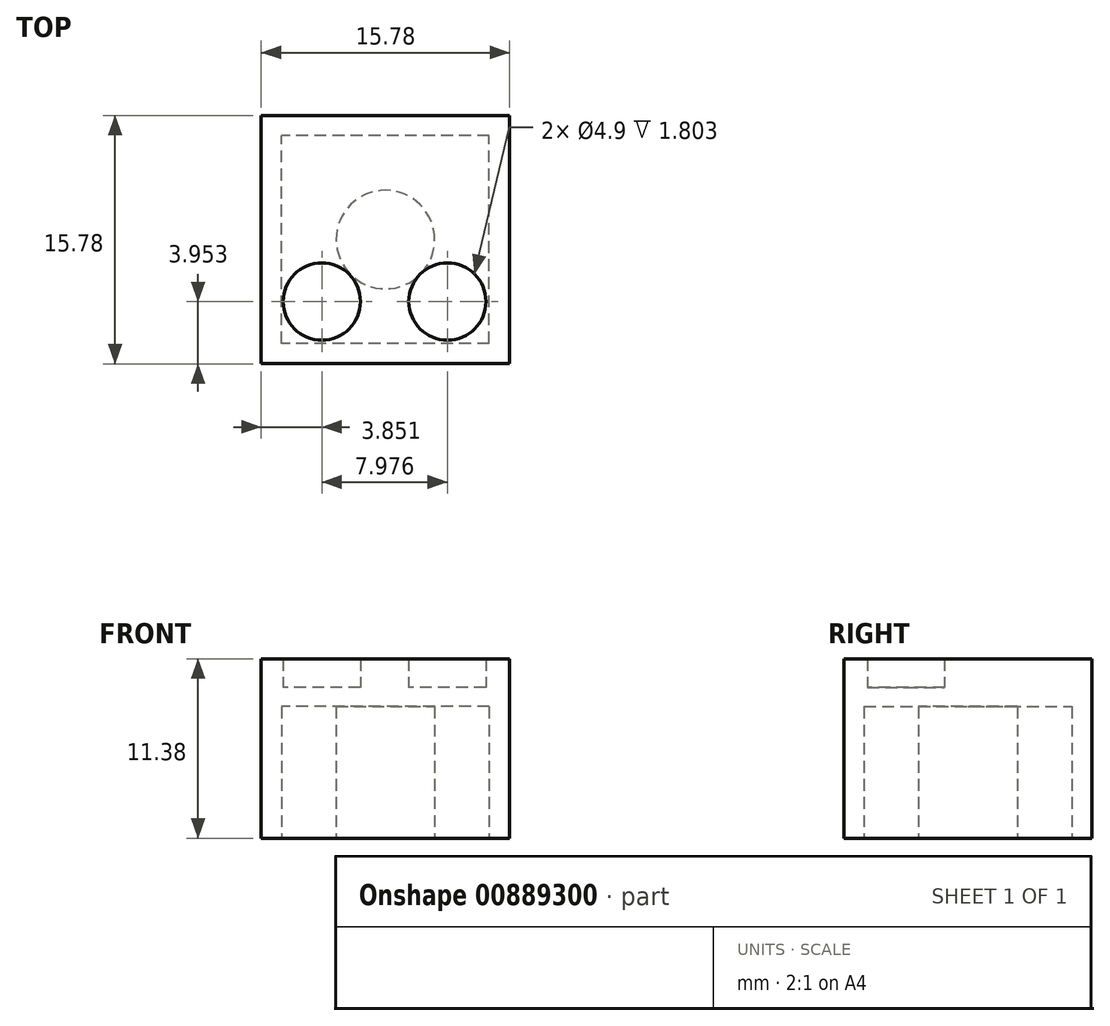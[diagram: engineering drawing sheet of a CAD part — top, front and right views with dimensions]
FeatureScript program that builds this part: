
annotation { "Feature Type Name" : "Feature", "Feature Type Description" : "" }
export const myFeature = defineFeature(function(context is Context, id is Id, definition is map)
    precondition{}
    {
        {
            var Q0;
            Q0=qCreatedBy(makeId("Top.planeOp"),FACE);
            var sketch = newSketch(context, id + "F0", { "sketchPlane" : qUnion([Q0])});
            skLineSegment(sketch, "E0.bottom", {"start": v(7.89, 7.89) * mm, "end": v(-7.89, 7.89) * mm});
            skLineSegment(sketch, "E0.top", {"start": v(7.89, -7.89) * mm, "end": v(-7.89, -7.89) * mm});
            skLineSegment(sketch, "E0.left", {"start": v(7.89, 7.89) * mm, "end": v(7.89, -7.89) * mm});
            skLineSegment(sketch, "E0.right", {"start": v(-7.89, 7.89) * mm, "end": v(-7.89, -7.89) * mm});
            skPoint(sketch, "E0.middle", {"position": v(0, 0) * mm});
            skSolve(sketch);
        }
        {
            var Q0;
            Q0 = qSketchRegion(id + "F2", true);
            var Q1;
            Q1 = qSketchRegion(id + "F0", true);
            extrude(context, id + "F1", {"entities" : qUnion([Q0, Q1]), "offsetDistance" : 25.4 * mm, "depth" : 9.58 * mm});
        }
        {
            var Q0;
            Q0=makeQuery(id+"F1.opExtrude","CAP_FACE",FACE,{"disambiguationData":[OSD([sQuery(id+"F0.wireOp",EDGE,"E0.bottom"),sQuery(id+"F0.wireOp",EDGE,"E0.top"),sQuery(id+"F0.wireOp",EDGE,"E0.left"),sQuery(id+"F0.wireOp",EDGE,"E0.right")])],"isStart":false});
            var sketch = newSketch(context, id + "F2", { "sketchPlane" : qUnion([Q0])});
            skCircle(sketch, "E1", {"center": v(-4.04, 3.94) * mm, "radius": 2.45 * mm});
            skCircle(sketch, "E2.1.0.0", {"center": v(3.94, 3.94) * mm, "radius": 2.45 * mm});
            skLineSegment(sketch, "E2.direction1", {"start": v(-4.04, 3.94) * mm, "end": v(3.94, 3.94) * mm, "construction": true});
            skCircle(sketch, "E3.MirrorC", {"center": v(-4.04, -3.94) * mm, "radius": 2.45 * mm});
            skCircle(sketch, "E4.MirrorC", {"center": v(3.94, -3.94) * mm, "radius": 2.45 * mm});
            skSolve(sketch);
        }
        {
            var Q0;
            Q0=makeQuery(id+"F2.imprint","IMPRINT",FACE,{"disambiguationData":[TD([[makeQuery(id+"F2.imprint","IMPRINT",EDGE,{"derivedFrom":sQuery(id+"F2.wireOp",EDGE,"E3.MirrorC")}),-1.0]])]});
            var Q1;
            Q1=makeQuery(id+"F2.imprint","IMPRINT",FACE,{"disambiguationData":[TD([[makeQuery(id+"F2.imprint","IMPRINT",EDGE,{"derivedFrom":sQuery(id+"F2.wireOp",EDGE,"E4.MirrorC")}),-1.0]])]});
            var Q2;
            Q2=makeQuery(id+"F2.imprint","IMPRINT",FACE,{"disambiguationData":[TD([[makeQuery(id+"F2.imprint","IMPRINT",EDGE,{"derivedFrom":sQuery(id+"F2.wireOp",EDGE,"E2.1.0.0")}),1.0]])]});
            var Q3;
            Q3=makeQuery(id+"F2.imprint","IMPRINT",FACE,{"disambiguationData":[TD([[makeQuery(id+"F2.imprint","IMPRINT",EDGE,{"derivedFrom":sQuery(id+"F2.wireOp",EDGE,"E1")}),1.0]])]});
            extrude(context, id + "F3", {"entities" : qUnion([Q0, Q1, Q2, Q3]), "operationType" : NewBodyOperationType.ADD, "depth" : 1.8 * mm});
        }
        {
            var Q0;
            Q0=makeQuery(id+"F1.opExtrude","CAP_FACE",FACE,{"disambiguationData":[OSD([sQuery(id+"F0.wireOp",EDGE,"E0.bottom"),sQuery(id+"F0.wireOp",EDGE,"E0.top"),sQuery(id+"F0.wireOp",EDGE,"E0.left"),sQuery(id+"F0.wireOp",EDGE,"E0.right")])],"isStart":true});
            var sketch = newSketch(context, id + "F4", { "sketchPlane" : qUnion([Q0])});
            skCircle(sketch, "E5", {"center": v(0, 0) * mm, "radius": 3.13 * mm});
            skSolve(sketch);
        }
        {
            var Q0;
            Q0=makeQuery(id+"F4.imprint","IMPRINT",FACE,{"disambiguationData":[TD([[makeQuery(id+"F4.imprint","IMPRINT",EDGE,{"derivedFrom":sQuery(id+"F4.wireOp",EDGE,"E5")}),-1.0]])]});
            var sketch = newSketch(context, id + "F5", { "sketchPlane" : qUnion([Q0])});
            skLineSegment(sketch, "E6.bottom", {"start": v(6.6, 6.6) * mm, "end": v(-6.6, 6.6) * mm});
            skLineSegment(sketch, "E6.top", {"start": v(6.6, -6.6) * mm, "end": v(-6.6, -6.6) * mm});
            skLineSegment(sketch, "E6.left", {"start": v(6.6, 6.6) * mm, "end": v(6.6, -6.6) * mm});
            skLineSegment(sketch, "E6.right", {"start": v(-6.6, 6.6) * mm, "end": v(-6.6, -6.6) * mm});
            skPoint(sketch, "E6.middle", {"position": v(0, 0) * mm});
            skSolve(sketch);
        }
        {
            var Q0;
            Q0=makeQuery(id+"F5.imprint","IMPRINT",FACE,{"disambiguationData":[TD([[makeQuery(id+"F5.imprint","IMPRINT",EDGE,{"derivedFrom":sQuery(id+"F5.wireOp",EDGE,"E6.bottom")}),1.0]])]});
            extrude(context, id + "F6", {"entities" : qUnion([Q0]), "operationType" : NewBodyOperationType.REMOVE, "oppositeDirection" : true, "depth" : 8.36 * mm});
        }
    });
